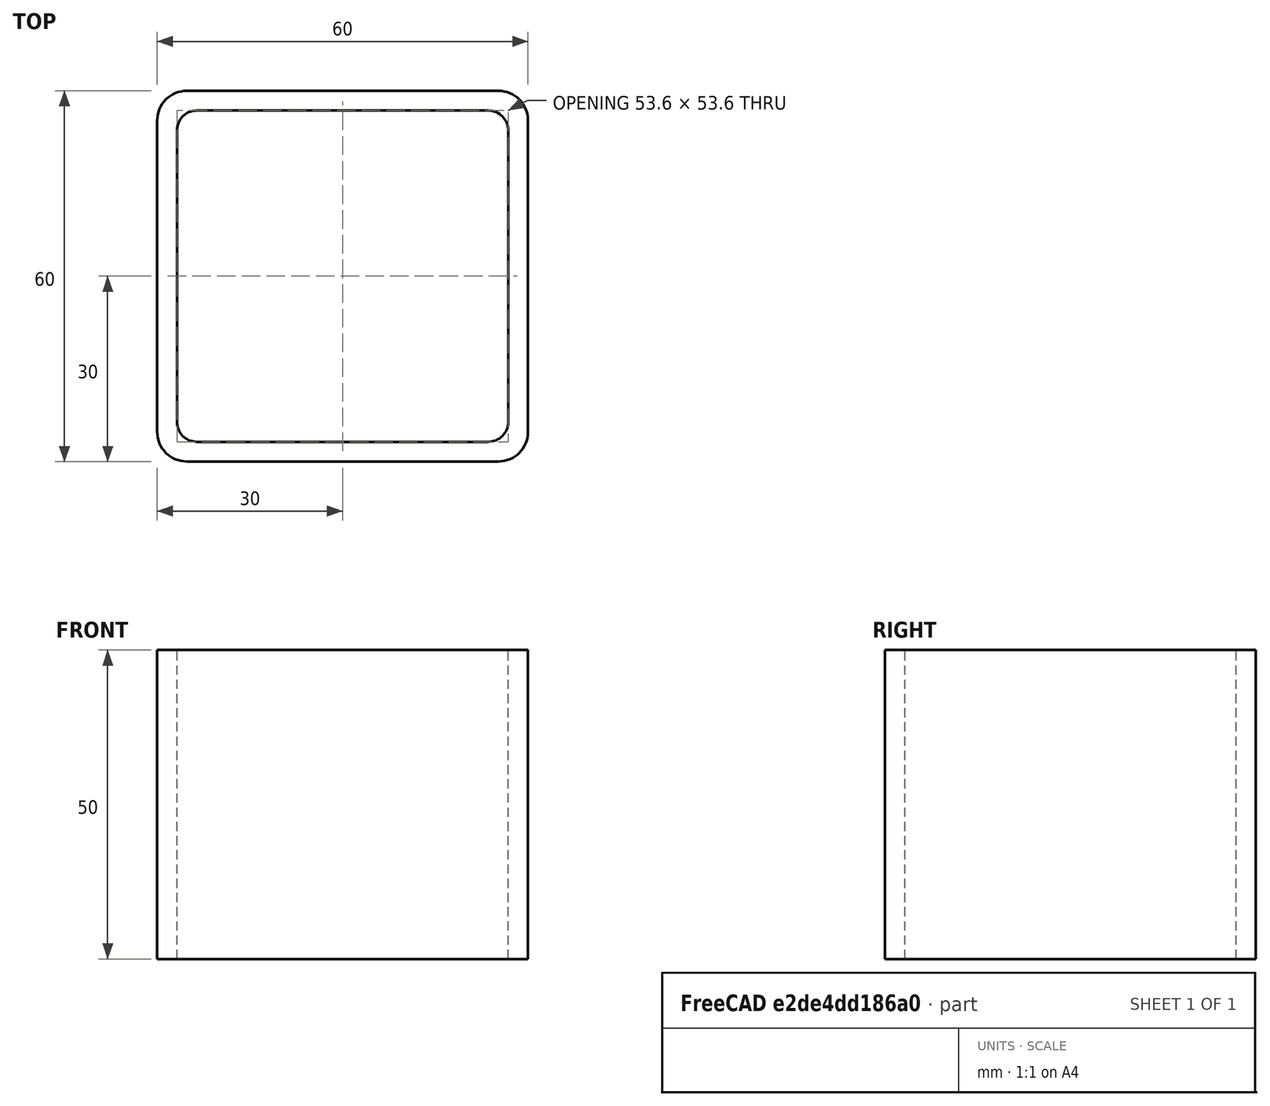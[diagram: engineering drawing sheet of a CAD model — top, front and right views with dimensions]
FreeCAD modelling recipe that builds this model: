
FCSTD DOCUMENT  (FreeCAD 0.15R4671 (Git))
Label: Square hollow section 60x60x3.2 EN10219 S235JRH
License: All rights reserved
LicenseURL: http://en.wikipedia.org/wiki/All_rights_reserved
objects: Sketcher::SketchObject×1, Part::Extrusion×1
note: 2 computed .brp shape members not serialized (recipe doc carries the construction recipe); baked Part::Feature solids carry a one-line shape summary decoded from their .brp

FEATURE [Sketcher::SketchObject] Sketch
  sketch-geometry (16):
    g0: LineSegment StartX=-23.6 StartY=26.8 StartZ=0 EndX=23.6 EndY=26.8 EndZ=0
    g1: LineSegment StartX=26.8 StartY=23.6 StartZ=0 EndX=26.8 EndY=-23.6 EndZ=0
    g2: LineSegment StartX=23.6 StartY=-26.8 StartZ=0 EndX=-23.6 EndY=-26.8 EndZ=0
    g3: LineSegment StartX=-26.8 StartY=-23.6 StartZ=0 EndX=-26.8 EndY=23.6 EndZ=0
    g4: LineSegment StartX=-25.2 StartY=30 StartZ=0 EndX=25.2 EndY=30 EndZ=0
    g5: LineSegment StartX=30 StartY=25.2 StartZ=0 EndX=30 EndY=-25.2 EndZ=0
    g6: LineSegment StartX=25.2 StartY=-30 StartZ=0 EndX=-25.2 EndY=-30 EndZ=0
    g7: LineSegment StartX=-30 StartY=-25.2 StartZ=0 EndX=-30 EndY=25.2 EndZ=0
    g8: ArcOfCircle CenterX=-23.6 CenterY=23.6 CenterZ=0 NormalX=0 NormalY=0 NormalZ=1 Radius=3.2 StartAngle=1.5708 EndAngle=3.14159
    g9: ArcOfCircle CenterX=23.6 CenterY=23.6 CenterZ=0 NormalX=0 NormalY=0 NormalZ=1 Radius=3.2 StartAngle=0 EndAngle=1.5708
    g10: ArcOfCircle CenterX=23.6 CenterY=-23.6 CenterZ=0 NormalX=0 NormalY=0 NormalZ=1 Radius=3.2 StartAngle=4.71239 EndAngle=6.28319
    g11: ArcOfCircle CenterX=-23.6 CenterY=-23.6 CenterZ=0 NormalX=0 NormalY=0 NormalZ=1 Radius=3.2 StartAngle=3.14159 EndAngle=4.71239
    g12: ArcOfCircle CenterX=25.2 CenterY=25.2 CenterZ=0 NormalX=0 NormalY=0 NormalZ=1 Radius=4.8 StartAngle=0 EndAngle=1.5708
    g13: ArcOfCircle CenterX=25.2 CenterY=-25.2 CenterZ=0 NormalX=0 NormalY=0 NormalZ=1 Radius=4.8 StartAngle=4.71239 EndAngle=6.28319
    g14: ArcOfCircle CenterX=-25.2 CenterY=-25.2 CenterZ=0 NormalX=0 NormalY=0 NormalZ=1 Radius=4.8 StartAngle=3.14159 EndAngle=4.71239
    g15: ArcOfCircle CenterX=-25.2 CenterY=25.2 CenterZ=0 NormalX=0 NormalY=0 NormalZ=1 Radius=4.8 StartAngle=1.5708 EndAngle=3.14159
  constraints (36):
    c: Horizontal(g2)
    c: Vertical(g3)
    c: Horizontal(g6)
    c: Vertical(g7)
    c: Tangent(g3,g8) = 1.5708
    c: Tangent(g0,g8) = 1.5708
    c: Tangent(g0,g9) = 1.5708
    c: Tangent(g1,g9) = 1.5708
    c: Tangent(g1,g10) = 1.5708
    c: Tangent(g2,g10) = 1.5708
    c: Tangent(g2,g11) = 1.5708
    c: Tangent(g3,g11) = 1.5708
    c: Tangent(g4,g12) = 1.5708
    c: Tangent(g5,g12) = 1.5708
    c: Tangent(g5,g13) = 1.5708
    c: Tangent(g6,g13) = 1.5708
    c: Tangent(g6,g14) = 1.5708
    c: Tangent(g7,g14) = 1.5708
    c: Tangent(g7,g15) = 1.5708
    c: Tangent(g4,g15) = 1.5708
    c: Equal(g9,g8)
    c: Equal(g9,g11)
    c: Equal(g9,g10)
    c: Equal(g12,g15)
    c: Equal(g12,g14)
    c: Equal(g12,g13)
    c: Symmetric(g4,g6,g-1)
    c: Symmetric(g7,g5,g-2)
    c: DistanceY(g4,g6) = -60
    c: DistanceX(g7,g5) = 60
    c: Symmetric(g3,g1,g-2)
    c: Symmetric(g0,g2,g-1)
    c: DistanceY(g0,g4) = 3.2
    c: DistanceX(g5,g1) = -3.2
    c: Radius(g9) = 3.2
    c: Radius(g12) = 4.8
FEATURE [Part::Extrusion] Extrude  label="Square hollow section 60x60x3.2 EN10219 S235JRH"
  Base = -> Sketch
  Dir = (0,0,50)
  Solid = true
